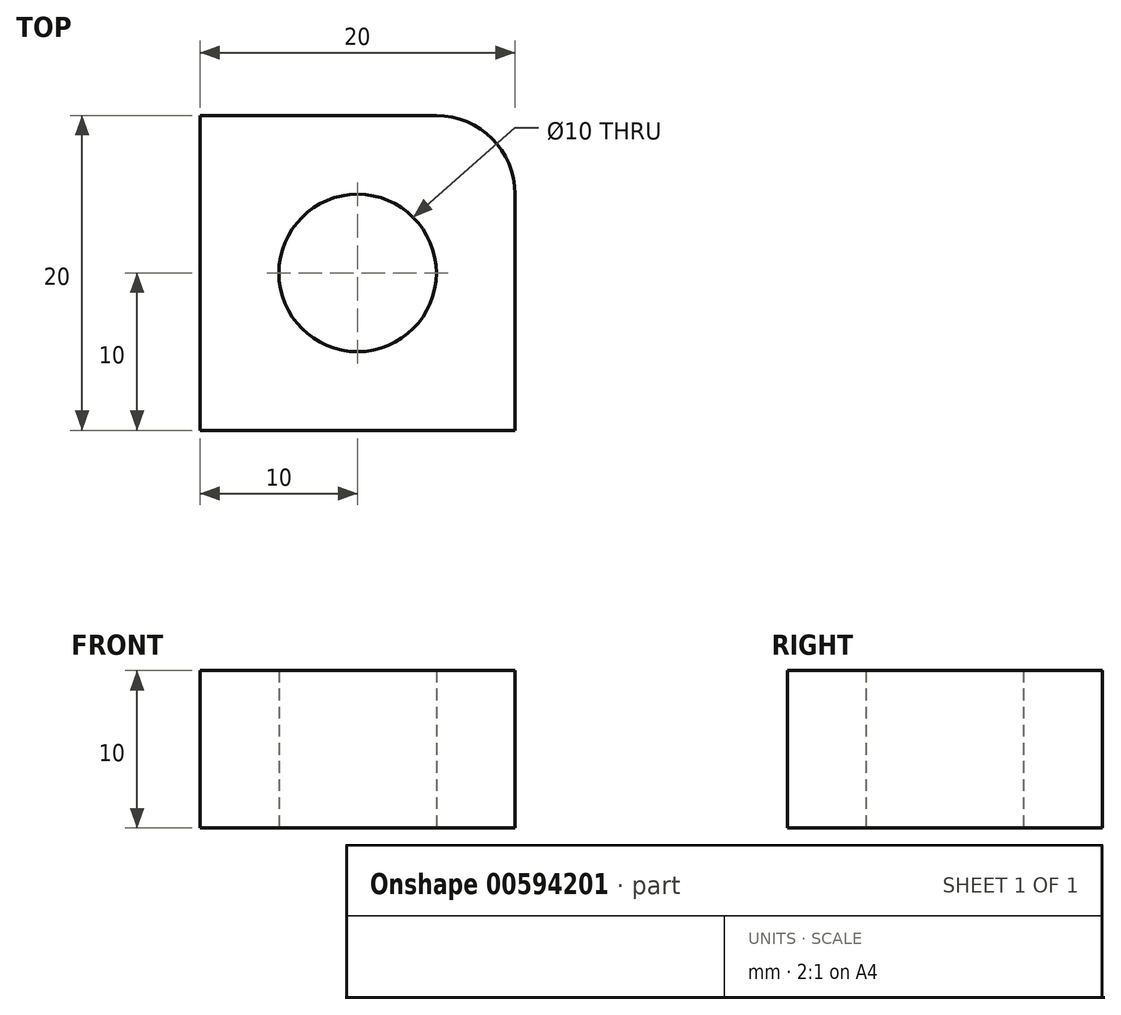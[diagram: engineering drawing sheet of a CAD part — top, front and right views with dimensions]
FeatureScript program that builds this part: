
annotation { "Feature Type Name" : "Feature", "Feature Type Description" : "" }
export const myFeature = defineFeature(function(context is Context, id is Id, definition is map)
    precondition{}
    {
        {
            var Q0;
            Q0=qCreatedBy(makeId("Top.planeOp"),FACE);
            var sketch = newSketch(context, id + "F0", { "sketchPlane" : qUnion([Q0])});
            skLineSegment(sketch, "E0.bottom", {"start": v(5, 10) * mm, "end": v(-10, 10) * mm});
            skLineSegment(sketch, "E0.top", {"start": v(10, -10) * mm, "end": v(-10, -10) * mm});
            skLineSegment(sketch, "E0.left", {"start": v(10, 5) * mm, "end": v(10, -10) * mm});
            skLineSegment(sketch, "E0.right", {"start": v(-10, 10) * mm, "end": v(-10, -10) * mm});
            skPoint(sketch, "E0.middle", {"position": v(0, 0) * mm});
            skCircle(sketch, "E1", {"center": v(0, 0) * mm, "radius": 5 * mm});
            skPoint(sketch, "E2.visualSharp", {"position": v(10, 10) * mm});
            skArc(sketch, "E2.filletArc", {"start": v(10, 5) * mm, "mid": v(8.54, 8.54) * mm, "end": v(5, 10) * mm});
            skSolve(sketch);
        }
        {
            var Q0;
            Q0=makeQuery(id+"F0.imprint","IMPRINT",FACE,{"disambiguationData":[TD([[makeQuery(id+"F0.imprint","IMPRINT",EDGE,{"derivedFrom":sQuery(id+"F0.wireOp",EDGE,"E0.bottom")}),1.0]])]});
            extrude(context, id + "F1", {"entities" : qUnion([Q0]), "depth" : 10 * mm, "offsetDistance" : 25 * mm});
        }
    });
